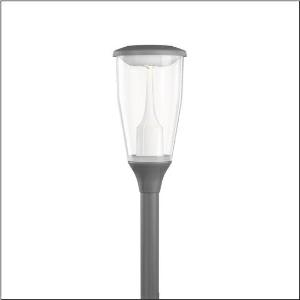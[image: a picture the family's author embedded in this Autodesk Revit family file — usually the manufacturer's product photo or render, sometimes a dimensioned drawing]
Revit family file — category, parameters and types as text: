
# Revit family: dl_11_iq___st1_2a_5xa5575af14hp00022_5e00
name_source: partatom
category: Lighting Fixtures
units: mm (PartAtom-declared; Revit-internal decimal feet)

## family parameters
Cut with Voids When Loaded = No
Host = Face
Light Source = No
Part Type = Normal
Room Calculation Point = No
Round Connector Dimension = Use Diameter
Shared = No

## types (1)
- --- (1 x LED, 4000 lm, 33.6 W, 2200K)
    Apparent Load = 34 VA
    CIE Flux Codes = 33 63 91 94 100
    Color Rendering = 70
    Color Temperature = 2200K
    Default Elevation = 1800 mm
    Description = DL 11 iQ, mast luminaire, Module 540 iQ-SR, primary light control with 3 zone facetted reflector, of plastic, silver coated, highly specular, structured, primary optical cover: cover, of PMMA, transparent, light distribution: ST1.2a, light emission: direct distribution, primary light characteristic: asymmetric, installation type: post-top, LED, High Power LED, rated luminous flux: 4.000lm, luminous efficacy: 119lm/W, light colour: 722, colour temperature: 2200K, control: Street-Remote, Auto-Match, Temp-Guard, Lumen-Switch, Night-Set, Smart-Wire, Light-Fading, Desk-Remote (wireless, voltage-free reading and setting of iQ features in the workshop via application-optimized NFC function/RFID function), optimised constant luminous flux control (CLO 2.0), mains connection: 220..240V, AC, 50/60Hz, connection cable pre-assembled, cable length: 5,5m, start of lifetime: 34W, end of service life: 36W, reduction: 15W, luminaire housing, upper part, of diecast aluminium, coated, Siteco® metallic grey (DB 702S), spigot size: 76mm (post-top), post-top mast mounting element, of diecast aluminium, coated, Siteco® metallic grey (DB 702S), Module 540 iQ-SR, traffic white (RAL 9016), equipment: Power, protection rating (complete): IP66, insulation class (complete): insulation class II (safety insulation), certification: CE, ENEC, ENEC+, VDE, packaging unit: 1 piece

Light Distribution: ST1.2a
    Height = 665 mm
    Lamp = 1 x LED
    Lamp Light Flux = 4000 lm
    Lamp Power = 33.6 W
    Lamp count = 1
    Length = 334 mm
    Luminous efficacy = 119 lm/W
    Manufacturer = Siteco
    ModVariant = No
    Model = 5XA5575AF14HP00022
    Number of Poles = 1
    OnlyDefault = Yes
    Power Factor = 1
    Product Name = DL 11 iQ | ST1.2a
    Product group = mast luminaire | pylon top
    ProductGroupID = 6100
    Protection Class = Protection class II
    Protection Degree = IP 66
    RLX_Detail_Level = 1
    RLX_Emergency_Light_Flux = 0 lm
    RLX_Emergency_Type = 0
    RLX_Emergency_Type_DB = No
    RlxData = <blob elided: 156197 chars, md5=01844472>
    Socket = socket
    Standby Power = 0 W
    System Light Flux = 4000 lm
    System Power = 34 W
    Type Comments = factory setting: luminous flux: 100 % | dim-lin: 254 | 695 mA
    Type Image = l_1258354.jpg
    URL = http://relux.com
    VarID = @adj_019959
    Voltage = 0 V
    Weight = 0.00 kg
    Width = 0 mm  [stored 0 ft]

note: [stored X ft] marks values corroborated as IEEE doubles in the binary element streams (Revit-internal decimal feet)

## geometry (parser evidence)
native form markers: Blend x4, Sweep x10
no freeform markers — native parametric forms only
